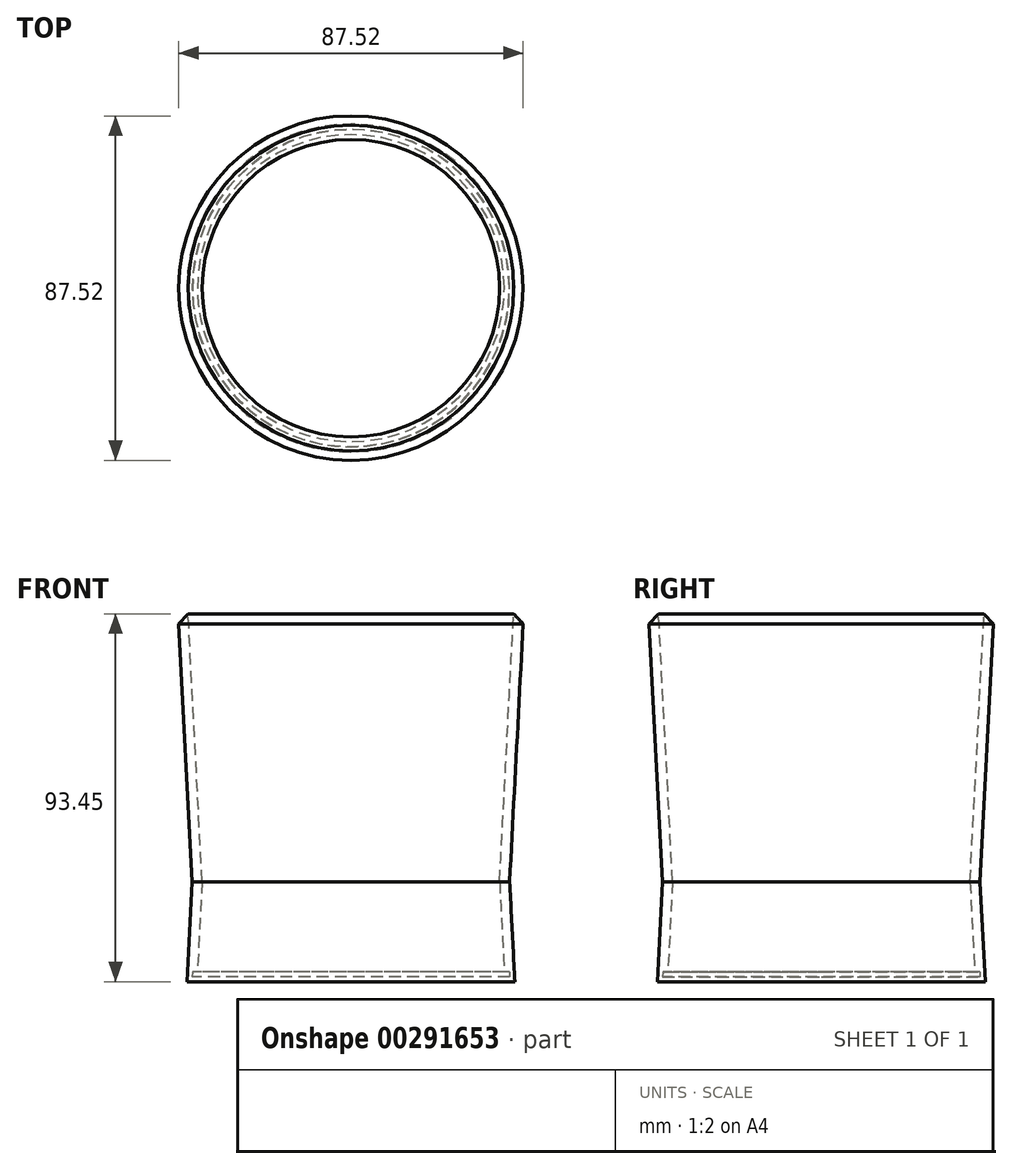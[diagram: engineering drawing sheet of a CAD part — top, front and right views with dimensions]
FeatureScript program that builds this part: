
annotation { "Feature Type Name" : "Feature", "Feature Type Description" : "" }
export const myFeature = defineFeature(function(context is Context, id is Id, definition is map)
    precondition{}
    {
        {
            var Q0;
            Q0=qCreatedBy(makeId("Top.planeOp"),FACE);
            var sketch = newSketch(context, id + "F0", { "sketchPlane" : qUnion([Q0])});
            skCircle(sketch, "E0", {"center": v(0, 0) * mm, "radius": 40.33 * mm});
            skSolve(sketch);
        }
        {
            var Q0;
            Q0=makeQuery(id+"F0.imprint","IMPRINT",FACE,{"disambiguationData":[TD([[makeQuery(id+"F0.imprint","IMPRINT",EDGE,{"derivedFrom":sQuery(id+"F0.wireOp",EDGE,"E0")}),1.0]])]});
            extrude(context, id + "F1", {"entities" : qUnion([Q0]), "depth" : 76.2 * mm, "hasDraft" : true, "draftAngle" : 3 * degree, "hasSecondDirection" : true, "secondDirectionOppositeDirection" : true, "secondDirectionDepth" : 25.4 * mm, "hasSecondDirectionDraft" : true, "secondDirectionDraftAngle" : 3 * degree});
        }
        {
            var Q0;
            Q0=makeQuery(id+"F1.opExtrude","CAP_FACE",FACE,{"disambiguationData":[OSD([sQuery(id+"F0.wireOp",EDGE,"E0")])],"isStart":false});
            shell(context, id + "F2", {"entities" : qUnion([Q0]), "thickness" : 2.54 * mm});
        }
        {
            var Q0;
            Q0=makeQuery(id+"F1.opExtrude","CAP_EDGE",EDGE,{"disambiguationData":[OSD([sQuery(id+"F0.wireOp",EDGE,"E0")])],"isStart":false});
            chamfer(context, id + "F3", {"entities" : qUnion([Q0]), "width" : 10.16 * mm, "tangentPropagation" : true});
        }
        {
            var Q0;
            {var subQ0=sQuery(id+"F0.wireOp",EDGE,"E0");Q0=makeQuery(id+"F2.opShell","OFFSET_FACE",FACE,{"disambiguationData":[OSD([subQ0]),TDD([makeQuery(id+"F1.opExtrude","CAP_FACE",FACE,{"disambiguationData":[OSD([subQ0])],"isStart":true})])]});}
            shell(context, id + "F4", {"entities" : qUnion([Q0]), "thickness" : 1.27 * mm});
        }
    });
